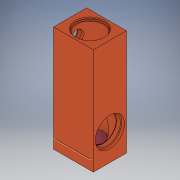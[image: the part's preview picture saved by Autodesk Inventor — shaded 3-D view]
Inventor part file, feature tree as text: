
AUTODESK INVENTOR PART (.ipt)
format: ipt  version: 2018 (Build 220112000, 112)  size: 178,688 bytes
history: native  units: in
note: dims shown in document units (in); Inventor stores cm internally (conversion verified against a paired STEP export)
features: sketch x10, extrude x9, plane x1, hole x1
ambient origin geometry x8: Origin, YZ Plane, XZ Plane, XY Plane, X Axis, Y Axis, Z Axis, Center Point
bodies: Solid1 (feature_tree)
feature tree (21):
  extrude  "Extrusion1"  Depth=1.25in
  plane  "Work Plane1"
  hole  "Hole1"  [1 undecoded]
  extrude  "Extrusion2"  Depth=1.1in
  extrude  "Extrusion4"  Depth=0.5in
  extrude  "Extrusion5"  Depth=4.0in TaperAngle=0.0deg
  extrude  "Extrusion3"  Depth=0.25in TaperAngle=0.0deg
  extrude  "Extrusion7"  Depth=4.0in TaperAngle=0.0deg
  extrude  "Extrusion8"  Depth=0.05in TaperAngle=0.0deg
  extrude  "Extrusion9"  Depth=0.2in TaperAngle=0.0deg
  extrude  "Extrusion10"  Depth=0.05in
  sketch  "Sketch1"  dims[d0=1.5in d1=1.25in]
  sketch  "Sketch2"  dims[d2=4.0in d3=0.0in]
  sketch  "Sketch3"  dims[d4=1.0in d5=0.75in d6=0.375in d7=0.25in d8=0.5635in d9=4.0in d10=0.8108in d11=-0.4in]
  sketch  "Sketch4"  dims[d12=1.0in d13=1.1in]
  sketch  "Sketch5"  dims[d14=0.1in d15=0.0in d16=0.5in]
  sketch  "Sketch6"  dims[d17=0.45in d18=4.0in d19=0.0in]
  sketch  "Sketch7"  dims[d20=1.0in d21=0.25in d22=0.0in]
  sketch  "Sketch8"  dims[d23=0.97in d24=4.0in d25=0.0in]
  sketch  "Sketch9"  dims[d26=0.55in d29=0.05in d30=0.0in]
  sketch  "Sketch10"  dims[d31=0.5in d32=0.2in d33=0.0in d34=1.05in d35=0.1in d36=0.0in d37=1.1in d38=0.05in d39=0.0in]
note: 1 required parameter value undecoded (feature->parameter linkage not recoverable at this tier; creation-order binding heuristic only, values carry confidence <= 0.55)
